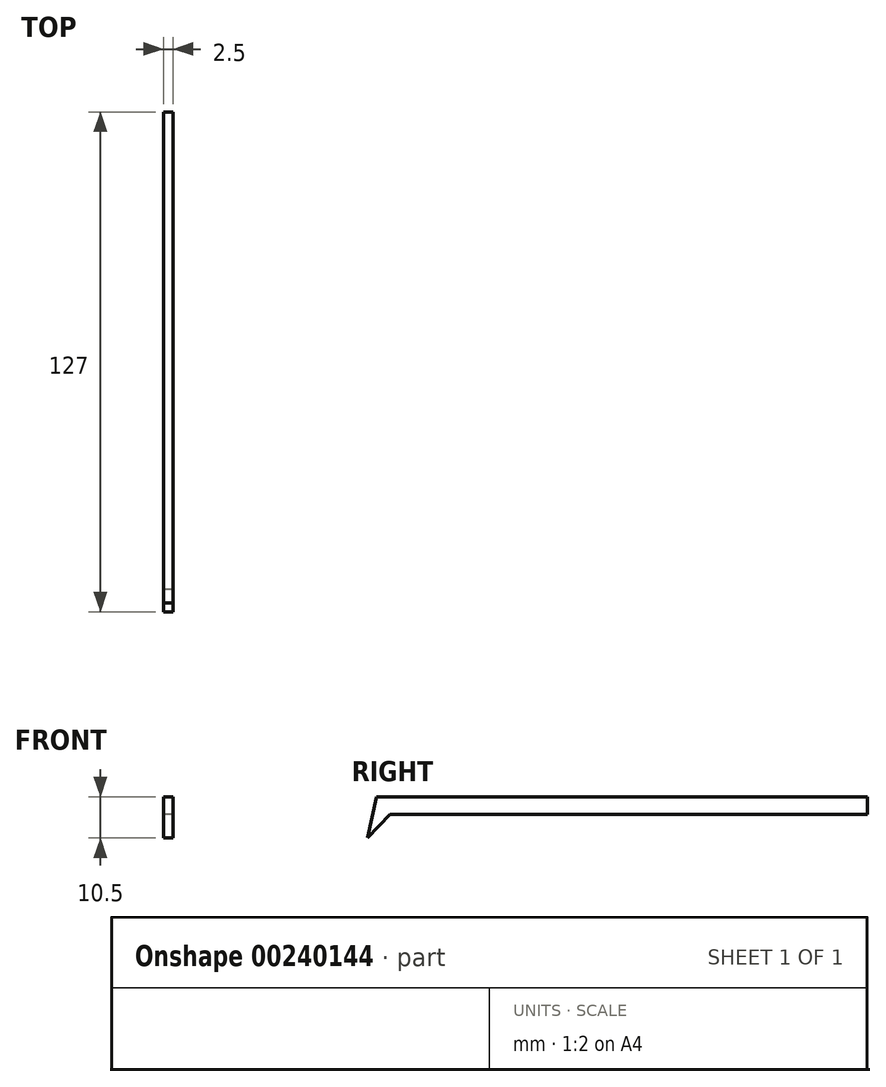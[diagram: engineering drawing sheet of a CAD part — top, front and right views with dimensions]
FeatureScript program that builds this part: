
annotation { "Feature Type Name" : "Feature", "Feature Type Description" : "" }
export const myFeature = defineFeature(function(context is Context, id is Id, definition is map)
    precondition{}
    {
        {
            var Q0;
            Q0=qCreatedBy(makeId("Right.planeOp"),FACE);
            var sketch = newSketch(context, id + "F0", { "sketchPlane" : qUnion([Q0])});
            skLineSegment(sketch, "E0", {"start": v(-12.57, 0) * mm, "end": v(112.18, 0) * mm});
            skLineSegment(sketch, "E1", {"start": v(112.18, -4.5) * mm, "end": v(-9.1, -4.5) * mm});
            skLineSegment(sketch, "E2", {"start": v(-9.1, -4.5) * mm, "end": v(-14.82, -10.5) * mm});
            skLineSegment(sketch, "E3", {"start": v(-14.82, -10.5) * mm, "end": v(-12.57, 0) * mm});
            skLineSegment(sketch, "E4", {"start": v(112.18, -4.5) * mm, "end": v(112.18, 0) * mm});
            skSolve(sketch);
        }
        {
            var Q0;
            Q0=makeQuery(id+"F0.imprint","IMPRINT",FACE,{"disambiguationData":[TD([[makeQuery(id+"F0.imprint","IMPRINT",EDGE,{"derivedFrom":sQuery(id+"F0.wireOp",EDGE,"E0")}),-1.0]])]});
            extrude(context, id + "F1", {"entities" : qUnion([Q0]), "depth" : 2.5 * mm});
        }
    });
